# Revit family: PDR
name_source: partatom
category: Air Terminals
revit_build: Autodesk Revit MEP 2012 (Build: 20110309_2315(x64)
units: mm (PartAtom-declared; Revit-internal decimal feet)

## types (8) — shared parameters
Alto base = 5/8"
Alto plato = 2 1/2"
Manufacturer = INNES
Max Flow = 0 CFM
Min Flow = 0 CFM
Máxima presión estática = 0.00 in-wg
Máxima velocidad de cuello = 0 FPM
Mínima presión estática = 0.00 in-wg
Mínima velocidad de cuello = 0 FPM
URL = http://www.innes.com.mx

## per-type parameters (varying)
| type | A cuello | B plato | Base 1 | Base 2 | Cuello Cuadrado | Cuello Redondo | Diametro interior | Radio |
| PDI-C-06-12 | 5 7/8" | 11 3/4" | 11" | 10 3/8" | Yes | No | 2 13/16" | 2 15/16" |
| PDI-C-08-16 | 7 7/8" | 15 3/4" | 15" | 14" | Yes | Yes | 3 13/16" | 3 15/16" |
| PDI-C-10-20 | 9 7/8" | 19 3/4" | 19" | 18" | Yes | Yes | 4 13/16" | 4 15/16" |
| PDI-C-08-20 | 7 7/8" | 19 3/4" | 19" | 18" | Yes | Yes | 3 13/16" | 3 15/16" |
| PDI-C-10-24 | 9 7/8" | 23 3/4" | 23" | 22" | Yes | Yes | 4 13/16" | 4 15/16" |
| PDI-C-08-12 | 7 7/8" | 11 3/4" | 11" | 10 3/8" | No | Yes | 3 13/16" | 3 15/16" |
| PDI-C-10-16 | 9 7/8" | 15 3/4" | 15" | 14" | Yes | Yes | 4 13/16" | 4 15/16" |
| PDI-C-12-24 | 11 7/8" | 23 3/4" | 23" | 22" | No | Yes | 5 13/16" | 5 15/16" |

## geometry (parser evidence)
native form markers: Blend x4, Sweep x1
no freeform markers — native parametric forms only
